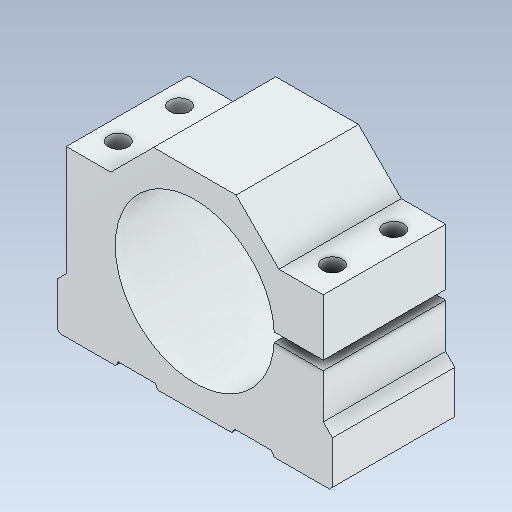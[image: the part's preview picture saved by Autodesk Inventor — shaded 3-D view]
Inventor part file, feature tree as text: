
AUTODESK INVENTOR PART (.ipt)
format: ipt  version: 2020.1 (Build 241239000, 239)  size: 160,256 bytes
history: native  units: mm
features: other x1, chamfer x1
ambient origin geometry x8: Origin, YZ Plane, XZ Plane, XY Plane, X Axis, Y Axis, Z Axis, Center Point
bodies: Body1 (feature_tree)
feature tree (2):
  other  "Твердое тело1"
  chamfer  "Chamfer2"  [1 undecoded]
note: 1 required parameter value undecoded (feature->parameter linkage not recoverable at this tier; creation-order binding heuristic only, values carry confidence <= 0.55)
